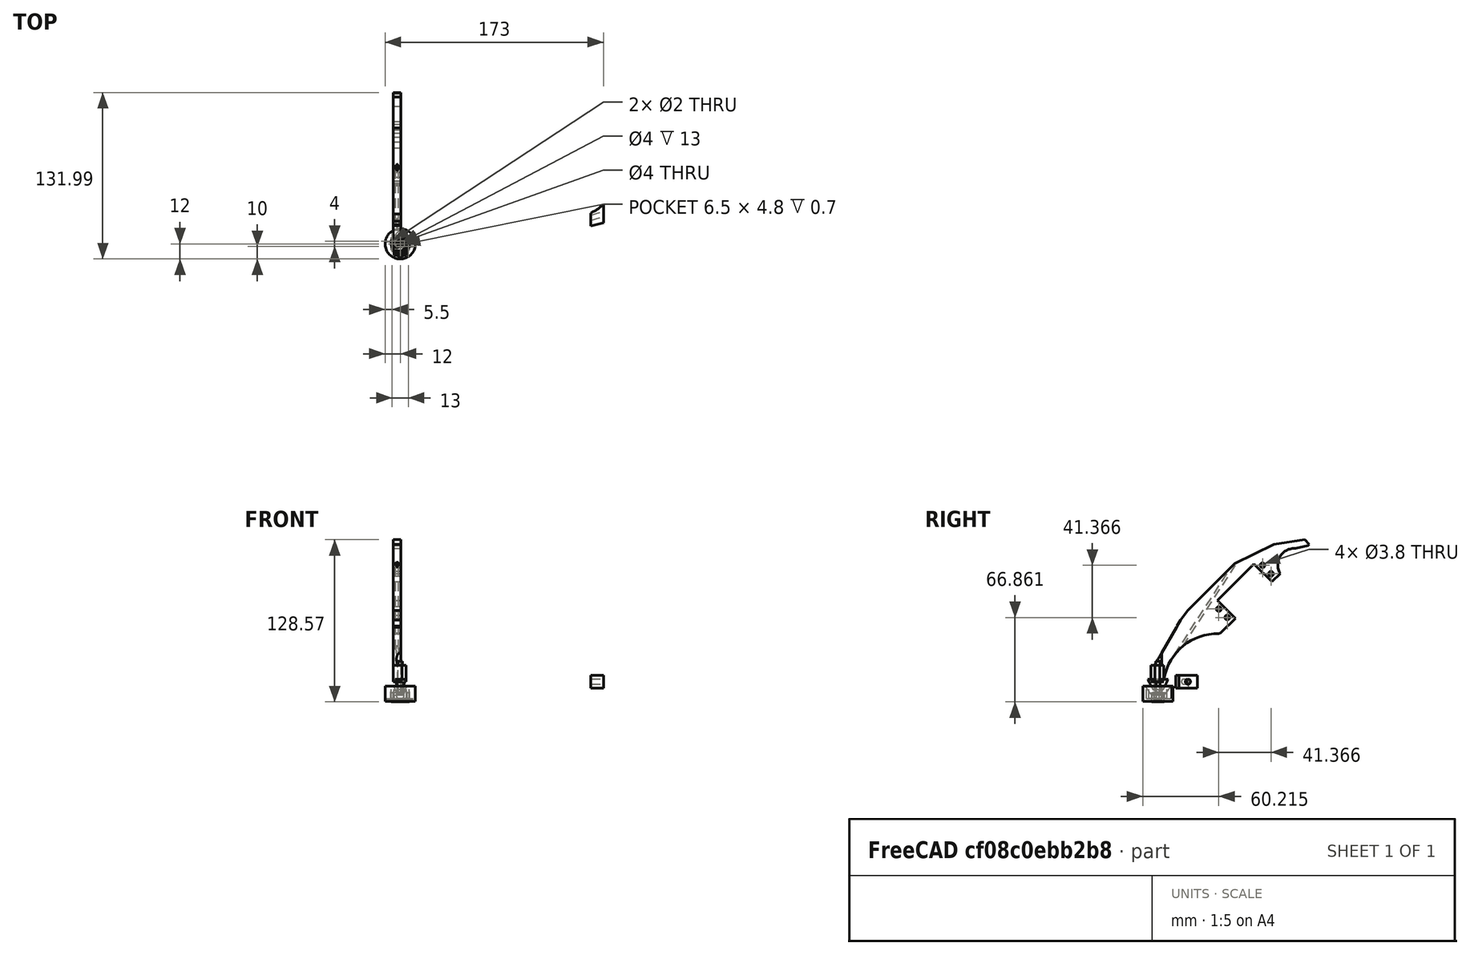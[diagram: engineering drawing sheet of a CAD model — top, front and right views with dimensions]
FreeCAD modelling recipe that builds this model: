
FCSTD DOCUMENT  (FreeCAD 0.16R6710 (Git))
Label: Feet sensors0.4
License: All rights reserved
LicenseURL: http://en.wikipedia.org/wiki/All_rights_reserved
objects: Part::Cut×43, Part::Cylinder×28, Part::Box×26, Part::Fuse×7, Part::Feature×5, Part::Chamfer×4, Part::Sphere×3, Part::MultiCommon×2, Part::Cone×2, Part::FeaturePython×2, Part::Fillet×2, App::DocumentObjectGroup×1
note: 124 computed .brp shape members not serialized (recipe doc carries the construction recipe); baked Part::Feature solids carry a one-line shape summary decoded from their .brp

FEATURE [Part::Sphere] Sphere
  Angle1 = -90
  Angle2 = 90
  Angle3 = 360
  Radius = 3
FEATURE [Part::Cylinder] Cylinder
  Angle = 360
  Height = 10
  Radius = 1.5
FEATURE [Part::Box] Box  label="Cube"
  Height = 1
  Length = 6.5
  Placement = pos=(-3.25,-2.4,-4.2) rot=(0,0,1;0rad)
  Width = 4.8
FEATURE [Part::Cylinder] Cylinder001
  Angle = 360
  Height = 10
  Placement = pos=(-11,2,-3.7) rot=(0,1,0;1.5708rad)
  Radius = 0.25
FEATURE [Part::Cylinder] Cylinder002
  Angle = 360
  Height = 10
  Placement = pos=(0,-2,-3.7) rot=(0,1,0;1.5708rad)
  Radius = 0.25
FEATURE [Part::Box] Box001  label="Cube001"
  Height = 7.25
  Length = 14
  Placement = pos=(-7,-5,-6) rot=(0,0,1;0rad)
  Width = 10
FEATURE [Part::Box] Box002  label="Cube002"
  Height = 1
  Length = 6.5
  Placement = pos=(-3.25,-2.4,-4.2) rot=(0,0,1;0rad)
  Width = 4.8
FEATURE [Part::Cylinder] Cylinder003
  Angle = 360
  Height = 10
  Placement = pos=(-11,2,-3.7) rot=(0,1,0;1.5708rad)
  Radius = 0.25
FEATURE [Part::Cylinder] Cylinder004
  Angle = 360
  Height = 10
  Placement = pos=(0,-2,-3.7) rot=(0,1,0;1.5708rad)
  Radius = 0.25
FEATURE [Part::Fuse] Fusion
  Base = -> Cylinder003
  Tool = -> Cylinder004
FEATURE [Part::Fuse] Fusion001
  Base = -> Box002
  Tool = -> Fusion
FEATURE [Part::Box] Box003  label="Cube003"
  Height = 3
  Length = 10
  Placement = pos=(-5,-6,-3.5) rot=(0,0,1;0rad)
  Width = 12
FEATURE [Part::Cut] Cut
  Base = -> Box001
  Tool = -> Box003
FEATURE [Part::Cut] Cut001
  Base = -> Cut
  Tool = -> Fusion001
FEATURE [Part::Fuse] Fusion002
  Base = -> Cylinder001
  Tool = -> Cylinder002
FEATURE [Part::Fuse] Fusion003  label="Switch"
  Base = -> Box
  Tool = -> Fusion002
FEATURE [Part::Box] Box004  label="Cube004"
  Height = 5
  Length = 10
  Placement = pos=(-5,4,-3.55) rot=(0,0,1;0rad)
  Width = 3
FEATURE [Part::Sphere] Sphere001
  Angle1 = -90
  Angle2 = 90
  Angle3 = 360
  Radius = 3.1
FEATURE [Part::Cylinder] Cylinder005
  Angle = 360
  Height = 10
  Placement = pos=(0,0,0.5) rot=(0,0,1;0rad)
  Radius = 2.5
FEATURE [Part::Fuse] Fusion004
  Base = -> Sphere001
  Tool = -> Cylinder005
FEATURE [Part::Cut] Cut002
  Base = -> Cut001
  Tool = -> Fusion004
FEATURE [Part::Fuse] Fusion005  label="Ball and Screw"
  Base = -> Sphere
  Placement = pos=(0,0,-1) rot=(0,0,1;0rad)
  Tool = -> Cylinder
FEATURE [Part::Cut] Cut003
  Base = -> Cut001
  Tool = -> Fusion004
FEATURE [Part::Box] Box005  label="Cube005"
  Height = 8
  Length = 21
  Placement = pos=(-9,-7,-3.5) rot=(0,0,1;0rad)
  Width = 17
FEATURE [Part::Box] Box006  label="Cube006"
  Height = 12
  Length = 21
  Placement = pos=(-9,-7,-3.5) rot=(0,0,1;0rad)
  Width = 17
FEATURE [Part::Cut] Cut004  label="Bottom Switch holder"
  Base = -> Cut003
  Tool = -> Box005
FEATURE [Part::MultiCommon] Common  label="Ball and screw holder"
  Shapes = -> [Cut002,Box006]
FEATURE [Part::Cylinder] Cylinder006
  Angle = 360
  Height = 12
  Placement = pos=(0,0,-5.5) rot=(0,0,1;0rad)
  Radius = 12
FEATURE [Part::Box] Box007  label="Cube007"
  Height = 10
  Length = 10
  Placement = pos=(-5,-9,-3.5) rot=(0,0,1;0rad)
  Width = 20
FEATURE [Part::Cylinder] Cylinder007
  Angle = 360
  Height = 10
  Placement = pos=(0,0,-3.5) rot=(0,0,1;0rad)
  Radius = 7.1
FEATURE [Part::Cylinder] Cylinder008
  Angle = 360
  Height = 10
  Placement = pos=(0,0,-6.5) rot=(0,0,1;0rad)
  Radius = 7.1
FEATURE [Part::MultiCommon] Common002  label="Switch plate"
  Shapes = -> [Cut004,Cylinder008]
FEATURE [Part::Cylinder] Cylinder009
  Angle = 360
  Height = 13
  Placement = pos=(-6.5,2,-6) rot=(0,0,1;0rad)
  Radius = 1
FEATURE [Part::Cylinder] Cylinder010
  Angle = 360
  Height = 13
  Placement = pos=(6.5,-2,-6) rot=(0,0,1;0rad)
  Radius = 1
FEATURE [Part::Box] Box008  label="Cube008"
  Height = 12
  Length = 41
  Placement = pos=(42,14,-1) rot=(0,0,1;0rad)
  Width = 20
FEATURE [Part::Cylinder] Cylinder011
  Angle = 360
  Height = 12
  Placement = pos=(38,19.5,-1) rot=(0,0,1;0rad)
  Radius = 1.9
FEATURE [Part::Cylinder] Cylinder012
  Angle = 360
  Height = 12
  Placement = pos=(38,29,-1) rot=(0,0,1;0rad)
  Radius = 1.9
FEATURE [Part::Cylinder] Cylinder013
  Angle = 360
  Height = 12
  Placement = pos=(87,29,-1) rot=(0,0,1;0rad)
  Radius = 1.9
FEATURE [Part::Cylinder] Cylinder014
  Angle = 360
  Height = 12
  Placement = pos=(87,19.5,-1) rot=(0,0,1;0rad)
  Radius = 1.9
FEATURE [Part::Box] Box009  label="Cube009"
  Height = 6
  Length = 184
  Width = 34
FEATURE [Part::Box] Box010  label="Cube010"
  Height = 12
  Length = 37
  Width = 8
FEATURE [Part::Cylinder] Cylinder015
  Angle = 360
  Height = 10
  Placement = pos=(20,37,0) rot=(0,0,1;0rad)
  Radius = 13
FEATURE [Part::Cut] Cut008
  Base = -> Box009
  Tool = -> Box010
FEATURE [Part::Cut] Cut009
  Base = -> Cut008
  Tool = -> Cylinder015
FEATURE [Part::Cylinder] Cylinder016
  Angle = 360
  Height = 10
  Placement = pos=(132,63,0) rot=(0,0,1;0rad)
  Radius = 43
FEATURE [Part::Cut] Cut010
  Base = -> Cut009
  Tool = -> Cylinder016
FEATURE [Part::Box] Box011  label="Cube011"
  Height = 10
  Length = 41
  Placement = pos=(120,0,0) rot=(0,0,1;0rad)
  Width = 6
FEATURE [Part::Cut] Cut011
  Base = -> Cut010
  Tool = -> Box011
FEATURE [Part::Box] Box012  label="Cube012"
  Height = 10
  Length = 23
  Placement = pos=(161,0,0) rot=(0,0,1;0rad)
  Width = 17
FEATURE [Part::Cut] Cut012
  Base = -> Cut011
  Tool = -> Box012
FEATURE [Part::Box] Box013  label="Cube013"
  Height = 10
  Length = 13
  Placement = pos=(0,8,0) rot=(0,0,1;0rad)
  Width = 11
FEATURE [Part::Cut] Cut013
  Base = -> Cut012
  Tool = -> Box013
FEATURE [Part::Box] Box014  label="Cube014"
  Height = 10
  Length = 53
  Placement = pos=(-16,28,0) rot=(0,0,-1;0.628319rad)
  Width = 10
FEATURE [Part::Cut] Cut014
  Base = -> Cut013
  Tool = -> Box014
FEATURE [Part::Box] Box015  label="Cube015"
  Height = 10
  Length = 49
  Placement = pos=(16,5,0) rot=(0,0,-1;0.331613rad)
  Width = 10
FEATURE [Part::Cut] Cut015
  Base = -> Cut014
  Tool = -> Box015
FEATURE [Part::Box] Box016  label="Cube016"
  Height = 10
  Length = 76
  Placement = pos=(46,-7,0) rot=(0,0,1;0rad)
  Width = 10
FEATURE [Part::Cut] Cut016
  Base = -> Cut015
  Tool = -> Box016
FEATURE [Part::Box] Box017  label="Cube017"
  Height = 10
  Length = 65
  Placement = pos=(115,-7,0) rot=(0,0,1;0.261799rad)
  Width = 11
FEATURE [Part::Cut] Cut017
  Base = -> Cut016
  Tool = -> Box017
FEATURE [Part::Box] Box018  label="Cube018"
  Height = 10
  Length = 14
  Placement = pos=(174,10,0) rot=(0,0,1;0.279253rad)
  Width = 10
FEATURE [Part::Cut] Cut018
  Base = -> Cut017
  Tool = -> Box018
FEATURE [Part::Box] Box019  label="Cube019"
  Height = 10
  Length = 10
  Placement = pos=(106,-7,0) rot=(0,0,1;0.139626rad)
  Width = 10
FEATURE [Part::Cut] Cut019
  Base = -> Cut018
  Tool = -> Box019
FEATURE [Part::Cut] Cut020
  Base = -> Cut019
  Tool = -> Box008
FEATURE [Part::Cut] Cut021
  Base = -> Cut020
  Tool = -> Cylinder014
FEATURE [Part::Cut] Cut022
  Base = -> Cut021
  Tool = -> Cylinder013
FEATURE [Part::Cut] Cut023
  Base = -> Cut022
  Tool = -> Cylinder012
FEATURE [Part::Cut] Cut024
  Base = -> Cut023
  Tool = -> Cylinder011
FEATURE [Part::Chamfer] Chamfer
  Base = -> Cut024
  Edges = 1 edges r=6: [Edge36]
FEATURE [Part::Chamfer] Chamfer001
  Base = -> Chamfer
  Edges = 1 edges r=1: [Edge59]
FEATURE [Part::Box] Box020  label="Cube020"
  Height = 10
  Length = 10
  Placement = pos=(151,12,5) rot=(0,0,1;0rad)
  Width = 21
FEATURE [Part::Box] Box021  label="Cube021"
  Height = 13
  Length = 26
  Placement = pos=(161,15,-3) rot=(0,0,1;0rad)
  Width = 23
FEATURE [Part::Cut] Cut025
  Base = -> Chamfer001
  Placement = pos=(-5.5,-24,171) rot=(0,1,0;1.5708rad)
  Tool = -> Box021
FEATURE [Part::Cylinder] Cylinder017
  Angle = 360
  Height = 19
  Placement = pos=(132,63,0) rot=(0,0,1;0rad)
  Radius = 43
FEATURE [Part::Cut] Cut026
  Base = -> Box020
  Tool = -> Cylinder017
FEATURE [Part::Box] Box022  label="Cube022"
  Height = 20
  Length = 65
  Placement = pos=(115,-7,0) rot=(0,0,1;0.261799rad)
  Width = 11
FEATURE [Part::Cut] Cut027
  Base = -> Cut026
  Tool = -> Box022
FEATURE [Part::Cylinder] Cylinder018
  Angle = 360
  Height = 18
  Placement = pos=(146.076,19.1828,10) rot=(-0.146221,0.978386,0.146221;1.59265rad)
  Radius = 2
FEATURE [Part::Cut] Cut028
  Base = -> Cut027
  Tool = -> Cylinder018
FEATURE [Part::Cone] Cone
  Angle = 360
  Height = 7
  Placement = pos=(0,0,1) rot=(0,0,1;0rad)
  Radius1 = 3
  Radius2 = 5.5
FEATURE [Part::FeaturePython] Clone  label="Clone of Cone"  # Draft clone (typed FeaturePython)
  Objects = -> [Cone]
  Placement = pos=(0,0,0.5) rot=(0,0,1;0rad)
  Scale = (1,2,1)
FEATURE [Part::Box] Box023  label="Cube023"
  Height = 5.5
  Length = 10
  Placement = pos=(-5,-5,-6) rot=(0,0,1;0rad)
  Width = 10
FEATURE [Part::Cut] Cut029
  Base = -> Cylinder006
  Tool = -> Box023
FEATURE [Part::Cut] Cut030
  Base = -> Cut029
  Tool = -> Cylinder010
FEATURE [Part::Cut] Cut031
  Base = -> Cut030
  Tool = -> Cylinder009
FEATURE [Part::Cut] Cut032
  Base = -> Cut031
  Tool = -> Clone
FEATURE [Part::Cylinder] Cylinder019
  Angle = 360
  Height = 10
  Placement = pos=(0,0,-1) rot=(0,0,1;0rad)
  Radius = 1.5
FEATURE [Part::Cut] Cut033
  Base = -> Cut032
  Tool = -> Cylinder019
FEATURE [App::DocumentObjectGroup] Group  label="Not used"
  Group = -> [Box004,Common,Box007,Cylinder007,Cut028]
FEATURE [Part::Cone] Cone001
  Angle = 360
  Height = 11
  Placement = pos=(0,0,2) rot=(0,0,1;0rad)
  Radius1 = 2
  Radius2 = 4
FEATURE [Part::FeaturePython] Clone001  label="Clone of Cone001"  # Draft clone (typed FeaturePython)
  Objects = -> [Cone001]
  Placement = pos=(0,0,4) rot=(0,0,1;0rad)
  Scale = (1,2,0.75)
FEATURE [Part::Cylinder] Cylinder020
  Angle = 360
  Height = 16
  Placement = pos=(0,0,9) rot=(0,0,1;0rad)
  Radius = 2
FEATURE [Part::Sphere] Sphere002
  Angle1 = -90
  Angle2 = 90
  Angle3 = 360
  Placement = pos=(0,0,-1) rot=(0,0,1;0rad)
  Radius = 3
FEATURE [Part::Cut] Cut034  label="Foot"
  Base = -> Cut033
  Tool = -> Sphere002
FEATURE [Part::Cylinder] Cylinder021
  Angle = 360
  Height = 26
  Radius = 1.7
FEATURE [Part::Fillet] Fillet
  Base = -> Cut025
  Edges = 1 edges r=3: [Edge30]
FEATURE [Part::Cylinder] Cylinder022  label="Not used cylinder001"
  Angle = 360
  Height = 16
  Placement = pos=(0,-50,23) rot=(0,0,1;0rad)
  Radius = 3
FEATURE [Part::Fillet] Fillet001
  Base = -> Fillet
  Edges = 1 edges r=3: [Edge39]
FEATURE [Part::Box] Box024  label="Cube024"
  Height = 13
  Length = 10
  Placement = pos=(-5.5,-5.5,10) rot=(0,0,1;0rad)
  Width = 10
FEATURE [Part::Cut] Cut035
  Base = -> Fillet001
  Placement = pos=(0,-8,5) rot=(-1,0,0;0.785398rad)
  Tool = -> Cylinder022
FEATURE [Part::Cylinder] Cylinder023
  Angle = 360
  Height = 26
  Radius = 1.7
FEATURE [Part::Fuse] Fusion006
  Base = -> Box024
  Tool = -> Cut035
FEATURE [Part::Cylinder] Cylinder024
  Angle = 360
  Height = 16
  Placement = pos=(0,0,23) rot=(0,0,1;0rad)
  Radius = 3
FEATURE [Part::Cut] Cut036
  Base = -> Fusion006
  Tool = -> Cylinder024
FEATURE [Part::Cut] Cut037
  Base = -> Cut036
  Tool = -> Cylinder020
FEATURE [Part::Chamfer] Chamfer002
  Base = -> Cut037
  Edges = 1 edges r=3: [Edge13]
FEATURE [Part::Chamfer] Chamfer003
  Base = -> Chamfer002
  Edges = 1 edges r=3: [Edge21]
FEATURE [Part::Cylinder] Cylinder025
  Angle = 360
  Height = 96
  Placement = pos=(-2.5,14,31) rot=(-1,0,0;0.575959rad)
  Radius = 1
FEATURE [Part::Cut] Cut038  label="Leg"
  Base = -> Chamfer003
  Tool = -> Cylinder025
FEATURE [Part::Cylinder] Cylinder026
  Angle = 360
  Height = 16
  Placement = pos=(0,0,0.5) rot=(0,0,1;0rad)
  Radius = 2
FEATURE [Part::Cut] Cut039  label="Bottom of leg"
  Base = -> Clone001
  Tool = -> Cylinder026
FEATURE [Part::Cylinder] Cylinder027
  Angle = 360
  Height = 10
  Radius = 4
FEATURE [Part::Box] Box025  label="Cube025"
  Height = 10
  Length = 10
  Placement = pos=(2.75,-5,0) rot=(0,0,1;0rad)
  Width = 10
FEATURE [Part::Feature] Box025001
  Placement = pos=(5.70513,-0.11843,0) rot=(0,0,1;1.0472rad)
  shape: bbox 13.66 x 13.66 x 10 mm, 6 faces (baked)
FEATURE [Part::Feature] Box025002
  Placement = pos=(2.95513,4.88157,0) rot=(0,0,1;2.0944rad)
  shape: bbox 13.66 x 13.66 x 10 mm, 6 faces (baked)
FEATURE [Part::Feature] Box025003
  Placement = pos=(-2.75,5,0) rot=(0,0,1;3.14159rad)
  shape: bbox 10 x 10 x 10 mm, 6 faces (baked)
FEATURE [Part::Feature] Box025004
  Placement = pos=(-5.70513,0.11843,0) rot=(0,0,1;4.18879rad)
  shape: bbox 13.66 x 13.66 x 10 mm, 6 faces (baked)
FEATURE [Part::Feature] Box025005
  Placement = pos=(-2.95513,-4.88157,0) rot=(0,0,-1;1.0472rad)
  shape: bbox 13.66 x 13.66 x 10 mm, 6 faces (baked)
FEATURE [Part::Cut] Cut040
  Base = -> Cylinder027
  Tool = -> Box025
FEATURE [Part::Cut] Cut041
  Base = -> Cut040
  Tool = -> Box025001
FEATURE [Part::Cut] Cut042
  Base = -> Cut041
  Tool = -> Box025005
FEATURE [Part::Cut] Cut043
  Base = -> Cut042
  Tool = -> Box025004
FEATURE [Part::Cut] Cut044
  Base = -> Cut043
  Tool = -> Box025003
FEATURE [Part::Cut] Cut045
  Base = -> Cut044
  Tool = -> Box025002
